FCSTD DOCUMENT  (FreeCAD 0.22R36526 (Git))
Label: magnets
License: All rights reserved
LicenseURL: https://en.wikipedia.org/wiki/All_rights_reserved
objects: Sketcher::SketchObject×1, PartDesign::Body×1, Spreadsheet::Sheet×1, Part::FeaturePython×1
note: 2 computed .brp shape members not serialized (recipe doc carries the construction recipe); baked Part::Feature solids carry a one-line shape summary decoded from their .brp

FEATURE [Sketcher::SketchObject] Sketch
  FullyConstrained = true
  expr: Constraints[13] = 2 * pi * <<Spreadsheet>>.RadiusMagnet / <<Spreadsheet>>.NumberElements / <<Spreadsheet>>.LengthMagnetFactor
  expr: Constraints[17] = <<Spreadsheet>>.RadiusMagnet
  sketch-geometry (9):
    g0: LineSegment StartX=-19.635 StartY=30 StartZ=0 EndX=19.635 EndY=30 EndZ=0
    g1: LineSegment StartX=19.635 StartY=30 StartZ=0 EndX=19.635 EndY=28 EndZ=0
    g2: LineSegment StartX=-19.635 StartY=30 StartZ=0 EndX=-19.635 EndY=28 EndZ=0
    g3: ArcOfCircle CenterX=3.5e-15 CenterY=40 CenterZ=0 NormalX=0 NormalY=0 NormalZ=1 AngleXU=0 Radius=23.0115 StartAngle=3.69017 EndAngle=5.7346
    g4: LineSegment StartX=-19.635 StartY=30 StartZ=0 EndX=3.6e-15 EndY=3.6e-15 EndZ=0
    g5: LineSegment StartX=3.6e-15 StartY=3.6e-15 StartZ=0 EndX=19.635 EndY=30 EndZ=0
    g6: LineSegment StartX=3.6e-15 StartY=30 StartZ=0 EndX=3.6e-15 EndY=3.6e-15 EndZ=0
    g7: LineSegment StartX=3.5e-15 StartY=40 StartZ=0 EndX=3.6e-15 EndY=30 EndZ=0
    g8: LineSegment StartX=3.5e-15 StartY=40 StartZ=0 EndX=3.6e-15 EndY=30 EndZ=0
  constraints (24):
    c: Horizontal(g0)
    c: Coincident(g1,g0)
    c: Vertical(g1)
    c: Coincident(g2,g0)
    c: Vertical(g2)
    c: Coincident(g3,g2)
    c: Coincident(g3,g1)
    c: Coincident(g4,g0)
    c: Coincident(g4,g-1)
    c: Coincident(g5,g4)
    c: Coincident(g5,g0)
    c: Equal(g4,g5)
    c: Distance(g1) = 2
    c: Distance(g0) = 39.2699
    c: PointOnObject(g6,g0)
    c: Coincident(g6,g4)
    c: Vertical(g6)
    c: DistanceY(g6,g6) = 30
    c: Coincident(g7,g3)
    c: Coincident(g7,g6)
    c: Coincident(g8,g3)
    c: Coincident(g8,g6)
    c: DistanceY(g7,g7) = 10
    c: Equal(g2,g1)
FEATURE [PartDesign::Body] Body
  Group = -> [Sketch]
  Origin = -> Origin
FEATURE [Spreadsheet::Sheet] Spreadsheet
  cells = A2='Number Elements; B2(NumberElements)=4; A3='LengthMagnetFactor; B3(LengthMagnetFactor)=1.2; A4='RadiusMagnet; B4(RadiusMagnet)=30
FEATURE [Part::FeaturePython] Array  # Draft array (typed FeaturePython)
  AlwaysSyncPlacement = false
  Angle = 360
  ArrayType = 1
  Axis = (0,0,1)
  Base = -> Sketch
  Center = (0,0,0)
  Count = 4
  ExpandArray = false
  Fuse = false
  IntervalAxis = (0,0,0)
  IntervalX = (50,0,0)
  IntervalY = (0,50,0)
  IntervalZ = (0,0,50)
  NumberCircles = 3
  NumberPolar = 4
  NumberX = 2
  NumberY = 2
  NumberZ = 1
  PlacementList = 4 placements: [(0,0,0),(0,0,0),(0,0,0),(0,0,0)]
  RadialDistance = 50
  ScaleList = (4) [(1,1,1),(1,1,1),(1,1,1),(1,1,1)]
  Symmetry = 1
  TangentialDistance = 25
  expr: NumberPolar = Spreadsheet.NumberElements
